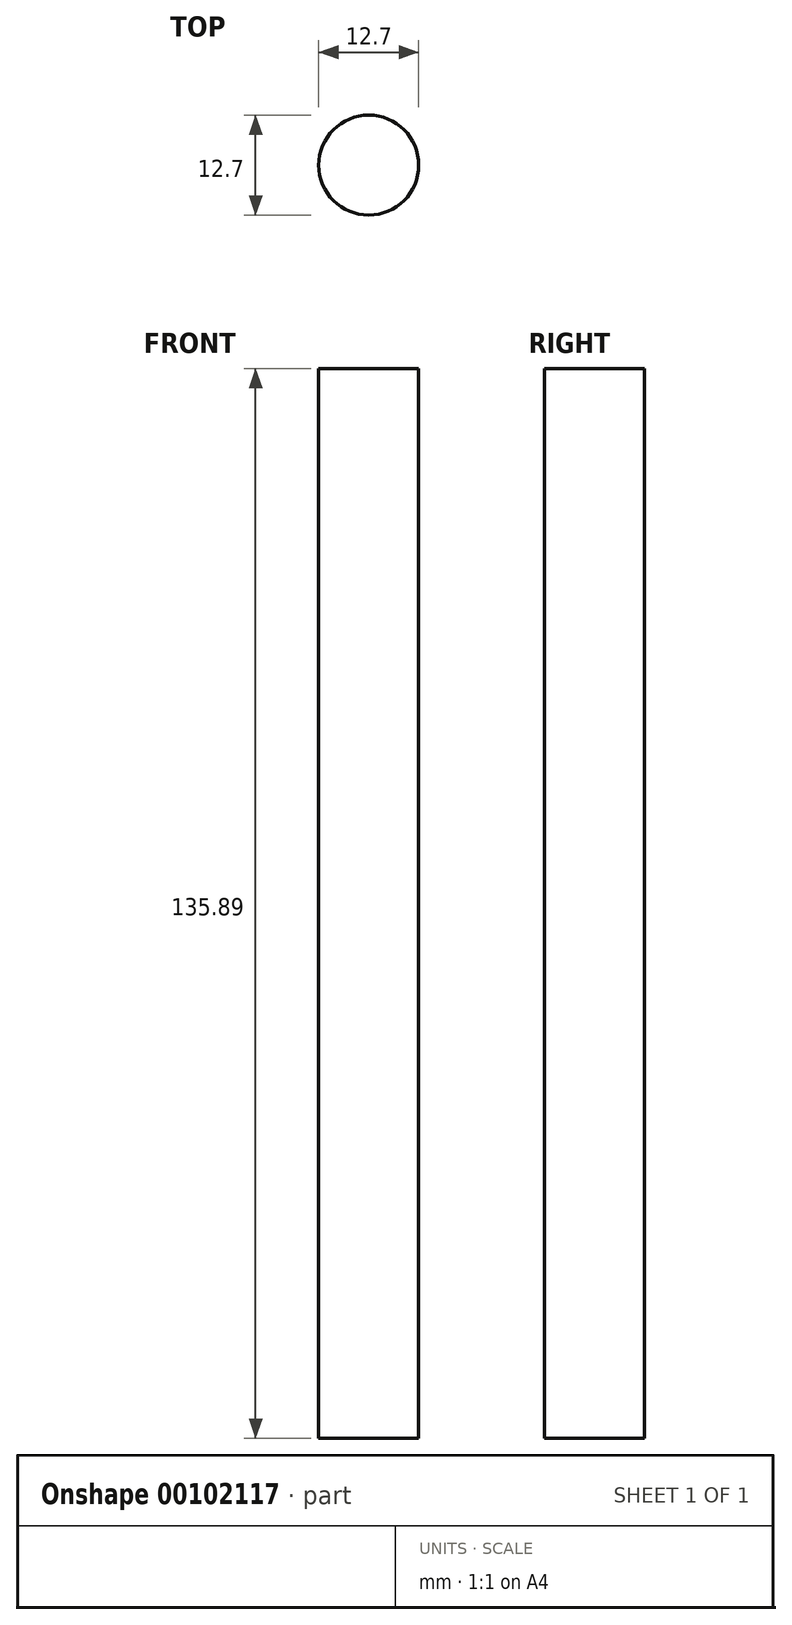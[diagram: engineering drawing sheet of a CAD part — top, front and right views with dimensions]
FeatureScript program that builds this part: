
annotation { "Feature Type Name" : "Feature", "Feature Type Description" : "" }
export const myFeature = defineFeature(function(context is Context, id is Id, definition is map)
    precondition{}
    {
        {
            var Q0;
            Q0=qCreatedBy(makeId("Top.planeOp"),FACE);
            var sketch = newSketch(context, id + "F0", { "sketchPlane" : qUnion([Q0])});
            skCircle(sketch, "E0", {"center": v(0, 0) * mm, "radius": 6.35 * mm});
            skSolve(sketch);
        }
        {
            var Q0;
            Q0 = qSketchRegion(id + "F0", true);
            extrude(context, id + "F1", {"entities" : qUnion([Q0]), "depth" : 135.89 * mm});
        }
    });
